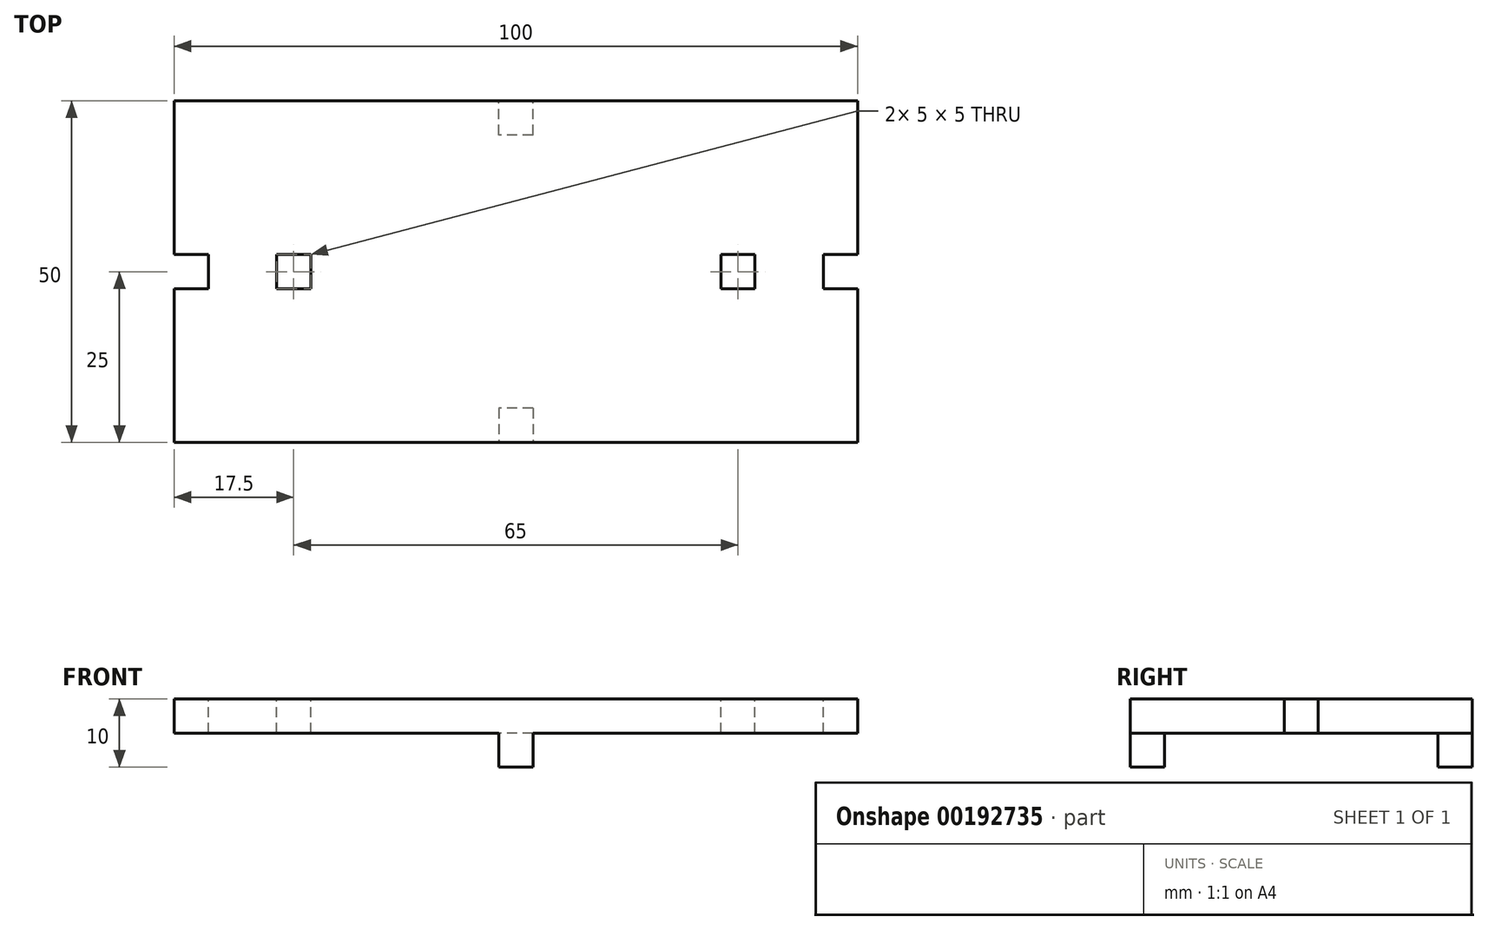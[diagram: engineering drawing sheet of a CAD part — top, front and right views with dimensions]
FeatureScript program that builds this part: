
annotation { "Feature Type Name" : "Feature", "Feature Type Description" : "" }
export const myFeature = defineFeature(function(context is Context, id is Id, definition is map)
    precondition{}
    {
        {
            var Q0;
            Q0=qCreatedBy(makeId("Top.planeOp"),FACE);
            var sketch = newSketch(context, id + "F0", { "sketchPlane" : qUnion([Q0])});
            skLineSegment(sketch, "E0.bottom", {"start": v(50, 25) * mm, "end": v(-50, 25) * mm});
            skLineSegment(sketch, "E0.top", {"start": v(50, -25) * mm, "end": v(-50, -25) * mm});
            skLineSegment(sketch, "E0.left", {"start": v(50, 25) * mm, "end": v(50, -25) * mm});
            skLineSegment(sketch, "E0.right", {"start": v(-50, 25) * mm, "end": v(-50, -25) * mm});
            skPoint(sketch, "E0.middle", {"position": v(0, 0) * mm});
            skSolve(sketch);
        }
        {
            var Q0;
            Q0 = qSketchRegion(id + "F0", true);
            extrude(context, id + "F1", {"entities" : qUnion([Q0]), "depth" : 5 * mm});
        }
        {
            var Q0;
            Q0=makeQuery(id+"F1.opExtrude","SWEPT_FACE",FACE,{"disambiguationData":[OSD([sQuery(id+"F0.wireOp",EDGE,"E0.top")])]});
            var sketch = newSketch(context, id + "F2", { "sketchPlane" : qUnion([Q0])});
            skLineSegment(sketch, "E1", {"start": v(-2.5, 0) * mm, "end": v(-2.5, -5) * mm});
            skLineSegment(sketch, "E2", {"start": v(-2.5, -5) * mm, "end": v(2.5, -5) * mm});
            skLineSegment(sketch, "E3", {"start": v(2.5, -5) * mm, "end": v(2.5, 0) * mm});
            skLineSegment(sketch, "E4", {"start": v(2.5, 0) * mm, "end": v(-2.5, 0) * mm});
            skSolve(sketch);
        }
        {
            var Q0;
            Q0 = qSketchRegion(id + "F2", true);
            extrude(context, id + "F3", {"entities" : qUnion([Q0]), "operationType" : NewBodyOperationType.ADD, "oppositeDirection" : true, "depth" : 5 * mm});
        }
        {
            var Q0;
            Q0=makeQuery(id+"F1.opExtrude","SWEPT_FACE",FACE,{"disambiguationData":[OSD([sQuery(id+"F0.wireOp",EDGE,"E0.bottom")])]});
            var sketch = newSketch(context, id + "F4", { "sketchPlane" : qUnion([Q0])});
            skLineSegment(sketch, "E5", {"start": v(-2.5, 0) * mm, "end": v(-2.5, -5) * mm});
            skLineSegment(sketch, "E6", {"start": v(-2.5, -5) * mm, "end": v(2.5, -5) * mm});
            skLineSegment(sketch, "E7", {"start": v(2.5, -5) * mm, "end": v(2.5, 0) * mm});
            skLineSegment(sketch, "E8", {"start": v(2.5, 0) * mm, "end": v(-2.5, 0) * mm});
            skSolve(sketch);
        }
        {
            var Q0;
            Q0 = qSketchRegion(id + "F4", true);
            extrude(context, id + "F5", {"entities" : qUnion([Q0]), "operationType" : NewBodyOperationType.ADD, "oppositeDirection" : true, "depth" : 5 * mm});
        }
        {
            var Q0;
            Q0=makeQuery(id+"F1.opExtrude","CAP_FACE",FACE,{"disambiguationData":[OSD([sQuery(id+"F0.wireOp",EDGE,"E0.bottom"),sQuery(id+"F0.wireOp",EDGE,"E0.top"),sQuery(id+"F0.wireOp",EDGE,"E0.left"),sQuery(id+"F0.wireOp",EDGE,"E0.right")])],"isStart":false});
            var sketch = newSketch(context, id + "F6", { "sketchPlane" : qUnion([Q0])});
            skLineSegment(sketch, "E9", {"start": v(0, 0) * mm, "end": v(-50, 0) * mm, "construction": true});
            skLineSegment(sketch, "E10", {"start": v(-50, 0) * mm, "end": v(-50, 2.5) * mm});
            skLineSegment(sketch, "E11", {"start": v(-50, 2.5) * mm, "end": v(-45, 2.5) * mm});
            skLineSegment(sketch, "E12", {"start": v(-45, 2.5) * mm, "end": v(-45, -2.5) * mm});
            skLineSegment(sketch, "E13", {"start": v(-45, -2.5) * mm, "end": v(-50, -2.5) * mm});
            skLineSegment(sketch, "E14", {"start": v(-50, -2.5) * mm, "end": v(-50, 0) * mm});
            skLineSegment(sketch, "E15.bottom", {"start": v(-35, 2.5) * mm, "end": v(-30, 2.5) * mm});
            skLineSegment(sketch, "E15.top", {"start": v(-35, -2.5) * mm, "end": v(-30, -2.5) * mm});
            skLineSegment(sketch, "E15.left", {"start": v(-35, 2.5) * mm, "end": v(-35, -2.5) * mm});
            skLineSegment(sketch, "E15.right", {"start": v(-30, 2.5) * mm, "end": v(-30, -2.5) * mm});
            skPoint(sketch, "E15.middle", {"position": v(-32.5, 0) * mm});
            skLineSegment(sketch, "E16", {"start": v(0, -25) * mm, "end": v(0, 25) * mm, "construction": true});
            skLineSegment(sketch, "E17.MirrorCS", {"start": v(30, 2.5) * mm, "end": v(30, -2.5) * mm});
            skLineSegment(sketch, "E18.MirrorCS", {"start": v(35, 2.5) * mm, "end": v(30, 2.5) * mm});
            skLineSegment(sketch, "E19.MirrorCS", {"start": v(35, 2.5) * mm, "end": v(35, -2.5) * mm});
            skLineSegment(sketch, "E20.MirrorCS", {"start": v(35, -2.5) * mm, "end": v(30, -2.5) * mm});
            skLineSegment(sketch, "E21.MirrorCS", {"start": v(45, -2.5) * mm, "end": v(50, -2.5) * mm});
            skLineSegment(sketch, "E22.MirrorCS", {"start": v(45, 2.5) * mm, "end": v(45, -2.5) * mm});
            skLineSegment(sketch, "E23.MirrorCS", {"start": v(50, -2.5) * mm, "end": v(50, 0) * mm});
            skLineSegment(sketch, "E24.MirrorCS", {"start": v(50, 0) * mm, "end": v(50, 2.5) * mm});
            skLineSegment(sketch, "E25.MirrorCS", {"start": v(50, 2.5) * mm, "end": v(45, 2.5) * mm});
            skSolve(sketch);
        }
        {
            var Q0;
            Q0 = qSketchRegion(id + "F6", true);
            extrude(context, id + "F7", {"entities" : qUnion([Q0]), "operationType" : NewBodyOperationType.REMOVE, "endBound" : BoundingType.UP_TO_NEXT, "oppositeDirection" : true, "depth" : 25 * mm});
        }
    });
